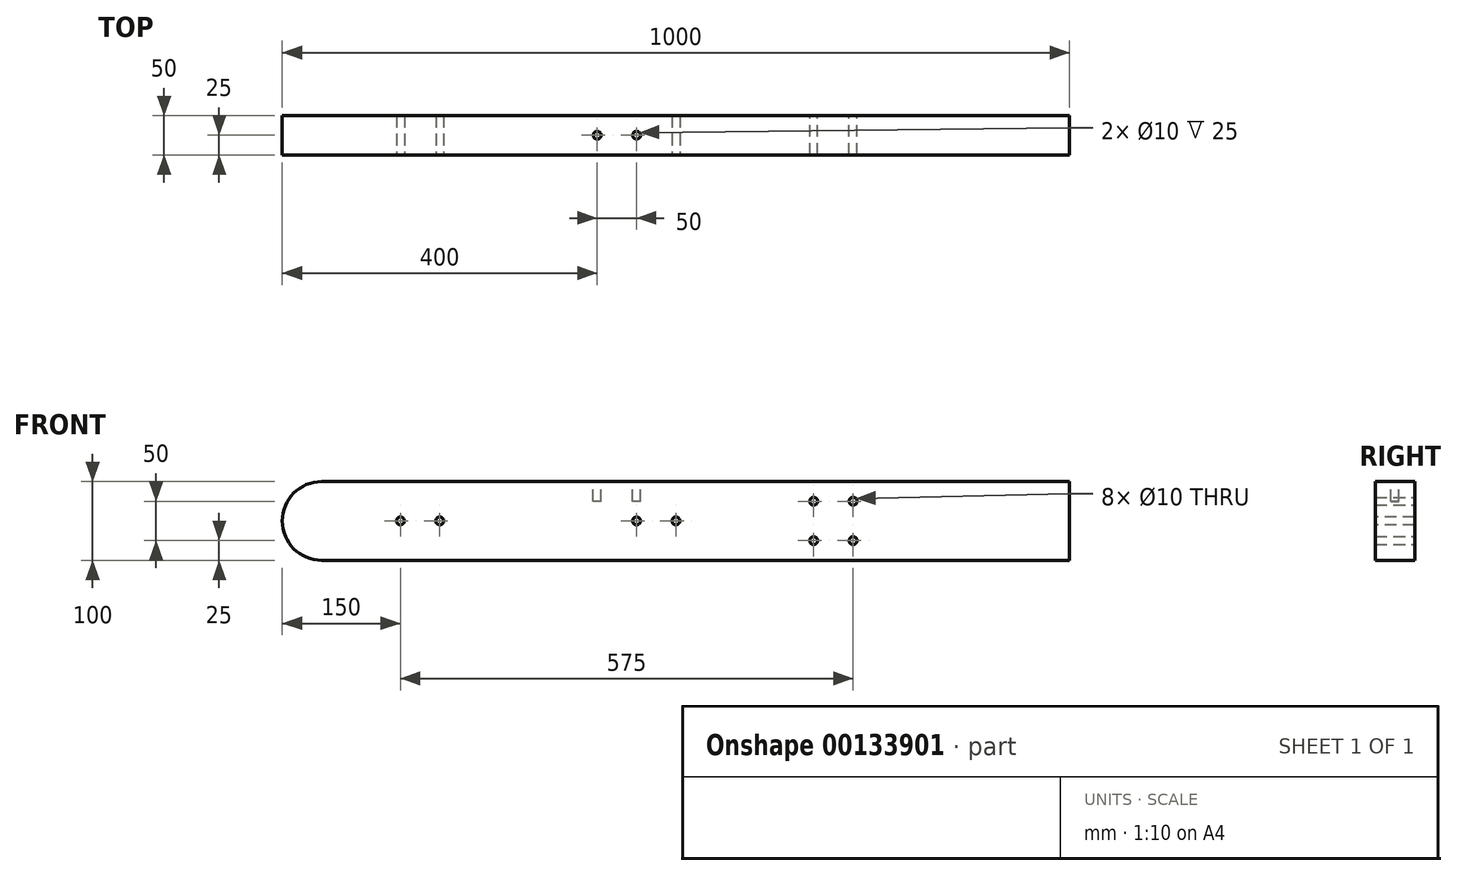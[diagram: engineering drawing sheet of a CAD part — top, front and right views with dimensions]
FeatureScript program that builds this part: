
annotation { "Feature Type Name" : "Feature", "Feature Type Description" : "" }
export const myFeature = defineFeature(function(context is Context, id is Id, definition is map)
    precondition{}
    {
        {
            var Q0;
            Q0=qCreatedBy(makeId("Front.planeOp"),FACE);
            var sketch = newSketch(context, id + "F0", { "sketchPlane" : qUnion([Q0])});
            skLineSegment(sketch, "E0.bottom", {"start": v(500, -50) * mm, "end": v(-500, -50) * mm});
            skLineSegment(sketch, "E0.top", {"start": v(500, 50) * mm, "end": v(-500, 50) * mm});
            skLineSegment(sketch, "E0.left", {"start": v(500, -50) * mm, "end": v(500, 50) * mm});
            skLineSegment(sketch, "E0.right", {"start": v(-500, -50) * mm, "end": v(-500, 50) * mm});
            skPoint(sketch, "E0.middle", {"position": v(0, 0) * mm});
            skSolve(sketch);
        }
        {
            var Q0;
            Q0=makeQuery(id+"F0.imprint","IMPRINT",FACE,{"disambiguationData":[TD([[makeQuery(id+"F0.imprint","IMPRINT",EDGE,{"derivedFrom":sQuery(id+"F0.wireOp",EDGE,"E0.bottom")}),-1.0]])]});
            extrude(context, id + "F1", {"entities" : qUnion([Q0]), "depth" : 50 * mm});
        }
        {
            var Q0;
            Q0=makeQuery(id+"F1.opExtrude","CAP_FACE",FACE,{"disambiguationData":[OSD([sQuery(id+"F0.wireOp",EDGE,"E0.bottom"),sQuery(id+"F0.wireOp",EDGE,"E0.top"),sQuery(id+"F0.wireOp",EDGE,"E0.left"),sQuery(id+"F0.wireOp",EDGE,"E0.right")])],"isStart":false});
            var sketch = newSketch(context, id + "F2", { "sketchPlane" : qUnion([Q0])});
            skCircle(sketch, "E1", {"center": v(-50, 0) * mm, "radius": 5 * mm});
            skCircle(sketch, "E2", {"center": v(0, 0) * mm, "radius": 5 * mm});
            skCircle(sketch, "E3", {"center": v(-350, 0) * mm, "radius": 5 * mm});
            skPoint(sketch, "E3.centerSnap0", {"position": v(-500, 0) * mm});
            skCircle(sketch, "E4", {"center": v(-300, 0) * mm, "radius": 5 * mm});
            skSolve(sketch);
        }
        {
            var Q0;
            Q0=makeQuery(id+"F1.opExtrude","SWEPT_FACE",FACE,{"disambiguationData":[OSD([sQuery(id+"F0.wireOp",EDGE,"E0.top")])]});
            var sketch = newSketch(context, id + "F3", { "sketchPlane" : qUnion([Q0])});
            skCircle(sketch, "E5", {"center": v(-100, -25) * mm, "radius": 5 * mm});
            skCircle(sketch, "E6", {"center": v(-50, -25) * mm, "radius": 5 * mm});
            skSolve(sketch);
        }
        {
            var Q0;
            Q0=makeQuery(id+"F3.imprint","IMPRINT",FACE,{"disambiguationData":[TD([[makeQuery(id+"F3.imprint","IMPRINT",EDGE,{"derivedFrom":sQuery(id+"F3.wireOp",EDGE,"E5")}),1.0]])]});
            var Q1;
            Q1=makeQuery(id+"F3.imprint","IMPRINT",FACE,{"disambiguationData":[TD([[makeQuery(id+"F3.imprint","IMPRINT",EDGE,{"derivedFrom":sQuery(id+"F3.wireOp",EDGE,"E6")}),1.0]])]});
            extrude(context, id + "F4", {"entities" : qUnion([Q0, Q1]), "operationType" : NewBodyOperationType.REMOVE, "oppositeDirection" : true, "depth" : 25 * mm});
        }
        {
            var Q0;
            Q0=makeQuery(id+"F2.imprint","IMPRINT",FACE,{"disambiguationData":[TD([[makeQuery(id+"F2.imprint","IMPRINT",EDGE,{"derivedFrom":sQuery(id+"F2.wireOp",EDGE,"E1")}),1.0]])]});
            var Q1;
            Q1=makeQuery(id+"F2.imprint","IMPRINT",FACE,{"disambiguationData":[TD([[makeQuery(id+"F2.imprint","IMPRINT",EDGE,{"derivedFrom":sQuery(id+"F2.wireOp",EDGE,"E2")}),1.0]])]});
            var Q2;
            Q2=makeQuery(id+"F2.imprint","IMPRINT",FACE,{"disambiguationData":[TD([[makeQuery(id+"F2.imprint","IMPRINT",EDGE,{"derivedFrom":sQuery(id+"F2.wireOp",EDGE,"E3")}),1.0]])]});
            var Q3;
            Q3=makeQuery(id+"F2.imprint","IMPRINT",FACE,{"disambiguationData":[TD([[makeQuery(id+"F2.imprint","IMPRINT",EDGE,{"derivedFrom":sQuery(id+"F2.wireOp",EDGE,"E4")}),1.0]])]});
            extrude(context, id + "F5", {"entities" : qUnion([Q0, Q1, Q2, Q3]), "operationType" : NewBodyOperationType.REMOVE, "oppositeDirection" : true, "depth" : 50 * mm});
        }
        {
            var Q0;
            Q0=makeQuery(id+"F1.opExtrude","CAP_FACE",FACE,{"disambiguationData":[OSD([sQuery(id+"F0.wireOp",EDGE,"E0.bottom"),sQuery(id+"F0.wireOp",EDGE,"E0.top"),sQuery(id+"F0.wireOp",EDGE,"E0.left"),sQuery(id+"F0.wireOp",EDGE,"E0.right")])],"isStart":true});
            var sketch = newSketch(context, id + "F6", { "sketchPlane" : qUnion([Q0])});
            skCircle(sketch, "E7", {"center": v(-225, -25) * mm, "radius": 5 * mm});
            skCircle(sketch, "E8", {"center": v(-175, -25) * mm, "radius": 5 * mm});
            skCircle(sketch, "E9", {"center": v(-225, 25) * mm, "radius": 5 * mm});
            skCircle(sketch, "E10", {"center": v(-175, 25) * mm, "radius": 5 * mm});
            skSolve(sketch);
        }
        {
            var Q0;
            Q0=makeQuery(id+"F6.imprint","IMPRINT",FACE,{"disambiguationData":[TD([[makeQuery(id+"F6.imprint","IMPRINT",EDGE,{"derivedFrom":sQuery(id+"F6.wireOp",EDGE,"E7")}),1.0]])]});
            var Q1;
            Q1=makeQuery(id+"F6.imprint","IMPRINT",FACE,{"disambiguationData":[TD([[makeQuery(id+"F6.imprint","IMPRINT",EDGE,{"derivedFrom":sQuery(id+"F6.wireOp",EDGE,"E8")}),1.0]])]});
            var Q2;
            Q2=makeQuery(id+"F6.imprint","IMPRINT",FACE,{"disambiguationData":[TD([[makeQuery(id+"F6.imprint","IMPRINT",EDGE,{"derivedFrom":sQuery(id+"F6.wireOp",EDGE,"E9")}),1.0]])]});
            var Q3;
            Q3=makeQuery(id+"F6.imprint","IMPRINT",FACE,{"disambiguationData":[TD([[makeQuery(id+"F6.imprint","IMPRINT",EDGE,{"derivedFrom":sQuery(id+"F6.wireOp",EDGE,"E10")}),1.0]])]});
            extrude(context, id + "F7", {"entities" : qUnion([Q0, Q1, Q2, Q3]), "operationType" : NewBodyOperationType.REMOVE, "oppositeDirection" : true, "depth" : 50 * mm});
        }
        {
            var Q0;
            Q0=makeQuery(id+"F1.opExtrude","SWEPT_EDGE",EDGE,{"disambiguationData":[OSD([sQuery(id+"F0.wireOp",EDGE,"E0.top"),sQuery(id+"F0.wireOp",EDGE,"E0.right")])]});
            var Q1;
            Q1=makeQuery(id+"F1.opExtrude","SWEPT_EDGE",EDGE,{"disambiguationData":[OSD([sQuery(id+"F0.wireOp",EDGE,"E0.bottom"),sQuery(id+"F0.wireOp",EDGE,"E0.right")])]});
            fillet(context, id + "F8", {"entities" : qUnion([Q0, Q1]), "radius" : 50 * mm, "tangentPropagation" : true, "allowEdgeOverflow" : false});
        }
    });
